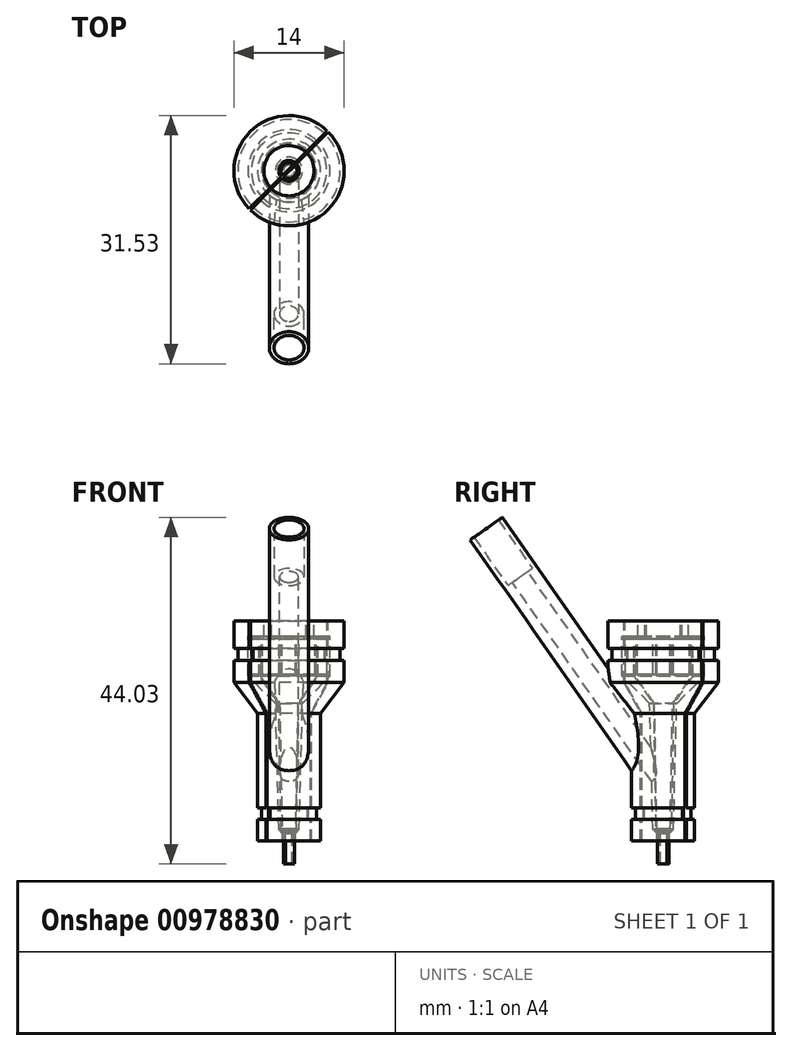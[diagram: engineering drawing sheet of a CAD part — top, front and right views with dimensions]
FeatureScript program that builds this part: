
annotation { "Feature Type Name" : "Feature", "Feature Type Description" : "" }
export const myFeature = defineFeature(function(context is Context, id is Id, definition is map)
    precondition{}
    {
        {
            var Q0;
            Q0=qCreatedBy(makeId("Front.planeOp"),FACE);
            var sketch = newSketch(context, id + "F0", { "sketchPlane" : qUnion([Q0])});
            skLineSegment(sketch, "E0", {"start": v(0, -7) * mm, "end": v(0.7, -7) * mm});
            skLineSegment(sketch, "E1", {"start": v(0.7, -7) * mm, "end": v(0.7, -2.83) * mm});
            skLineSegment(sketch, "E2", {"start": v(0.7, -2.83) * mm, "end": v(1, -2.83) * mm});
            skLineSegment(sketch, "E3", {"start": v(1, -2.83) * mm, "end": v(1, -2.58) * mm});
            skLineSegment(sketch, "E4", {"start": v(1, -2.58) * mm, "end": v(0, -2.58) * mm});
            skLineSegment(sketch, "E5", {"start": v(0, -2.58) * mm, "end": v(0, -7) * mm});
            skLineSegment(sketch, "E6", {"start": v(0, 0.49) * mm, "end": v(0, -9.16) * mm});
            skSolve(sketch);
        }
        {
            var Q0;
            Q0 = qSketchRegion(id + "F0", true);
            var Q1;
            Q1=sQuery(id+"F0.wireOp",EDGE,"E6");
            revolve(context, id + "F1", {"surfaceOperationType" : NewSurfaceOperationType.NEW, "entities" : qUnion([Q0]), "axis" : qUnion([Q1]), "revolveType" : RevolveType.FULL});
        }
        {
            var Q0;
            Q0=qCreatedBy(makeId("Front.planeOp"),FACE);
            var sketch = newSketch(context, id + "F2", { "sketchPlane" : qUnion([Q0])});
            skLineSegment(sketch, "E7", {"start": v(0.8, -3.1) * mm, "end": v(1.3, -2.6) * mm});
            skLineSegment(sketch, "E8", {"start": v(0.8, -3.1) * mm, "end": v(0.8, -4.1) * mm});
            skLineSegment(sketch, "E9", {"start": v(0.8, -4.1) * mm, "end": v(4, -4.1) * mm});
            skLineSegment(sketch, "E10", {"start": v(1.72, 13.38) * mm, "end": v(5.2, 16.87) * mm});
            skLineSegment(sketch, "E11", {"start": v(7, 23.87) * mm, "end": v(3.2, 23.87) * mm});
            skLineSegment(sketch, "E12", {"start": v(3.2, 21.87) * mm, "end": v(3.2, 23.87) * mm});
            skLineSegment(sketch, "E13", {"start": v(3.2, 21.87) * mm, "end": v(5.2, 21.87) * mm});
            skLineSegment(sketch, "E14", {"start": v(5.2, 21.87) * mm, "end": v(5.2, 16.87) * mm});
            skLineSegment(sketch, "E15", {"start": v(1.3, -2.6) * mm, "end": v(1.72, 13.38) * mm});
            skLineSegment(sketch, "E16.bottom", {"start": v(4.8, 21.59) * mm, "end": v(1.3, 21.59) * mm});
            skLineSegment(sketch, "E16.top", {"start": v(4.8, 17.09) * mm, "end": v(1.3, 17.09) * mm});
            skLineSegment(sketch, "E16.left", {"start": v(4.8, 21.59) * mm, "end": v(4.8, 17.09) * mm});
            skLineSegment(sketch, "E16.right", {"start": v(1.3, 21.59) * mm, "end": v(1.3, 17.09) * mm});
            skLineSegment(sketch, "E17", {"start": v(0, 34.31) * mm, "end": v(0, -20.8) * mm});
            skLineSegment(sketch, "E18", {"start": v(7, 23.87) * mm, "end": v(7, 20.36) * mm});
            skLineSegment(sketch, "E19", {"start": v(7, 20.36) * mm, "end": v(6.5, 20.36) * mm});
            skLineSegment(sketch, "E20", {"start": v(6.5, 20.36) * mm, "end": v(6.5, 18.86) * mm});
            skLineSegment(sketch, "E21", {"start": v(6.5, 18.86) * mm, "end": v(7, 18.86) * mm});
            skLineSegment(sketch, "E22", {"start": v(7, 18.86) * mm, "end": v(7, 16.04) * mm});
            skLineSegment(sketch, "E23", {"start": v(4, 12.13) * mm, "end": v(4, 0.13) * mm});
            skLineSegment(sketch, "E24", {"start": v(4, 0.13) * mm, "end": v(3.5, 0.14) * mm});
            skLineSegment(sketch, "E25", {"start": v(3.5, 0.14) * mm, "end": v(3.5, -1.36) * mm});
            skLineSegment(sketch, "E26", {"start": v(3.5, -1.36) * mm, "end": v(4, -1.37) * mm});
            skLineSegment(sketch, "E27", {"start": v(4, -1.37) * mm, "end": v(4, -4.1) * mm});
            skLineSegment(sketch, "E28", {"start": v(4, 12.13) * mm, "end": v(7, 16.04) * mm});
            skSolve(sketch);
        }
        {
            var Q0;
            Q0=makeQuery(id+"F2.imprint","IMPRINT",FACE,{"disambiguationData":[TD([[makeQuery(id+"F2.imprint","IMPRINT",EDGE,{"derivedFrom":sQuery(id+"F2.wireOp",EDGE,"E7")}),-1.0]])]});
            var Q1;
            Q1=makeQuery(id+"F2.imprint","IMPRINT",FACE,{"disambiguationData":[TD([[makeQuery(id+"F2.imprint","IMPRINT",EDGE,{"derivedFrom":sQuery(id+"F2.wireOp",EDGE,"E16.bottom")}),1.0]])]});
            var Q2;
            Q2=sQuery(id+"F2.wireOp",EDGE,"E17");
            revolve(context, id + "F3", {"surfaceOperationType" : NewSurfaceOperationType.NEW, "entities" : qUnion([Q0, Q1]), "axis" : qUnion([Q2]), "revolveType" : RevolveType.FULL});
        }
        {
            var Q0;
            Q0=sQuery(id+"F2.wireOp",EDGE,"E11");
            cPlane(context, id + "F4", {"entities" : qUnion([Q0]), "cplaneType" : CPlaneType.LINE_ANGLE, "offset" : 25 * mm, "angle" : 55 * degree, "width" : 150 * mm, "height" : 150 * mm});
        }
        {
            var Q0;
            Q0=qCreatedBy(id+"F4.planeOp",FACE);
            var sketch = newSketch(context, id + "F5", { "sketchPlane" : qUnion([Q0])});
            skCircle(sketch, "E29", {"center": v(0, 2) * mm, "radius": 1.05 * mm});
            skSolve(sketch);
        }
        {
            var Q0;
            Q0 = qSketchRegion(id + "F5", true);
            extrude(context, id + "F6", {"entities" : qUnion([Q0]), "operationType" : NewBodyOperationType.ADD, "depth" : 15 * mm, "offsetDistance" : 25 * mm, "hasSecondDirection" : true, "secondDirectionOppositeDirection" : true, "secondDirectionDepth" : -2 * mm});
        }
        {
            var Q0;
            Q0=makeQuery(id+"F6.opExtrude","CAP_FACE",FACE,{"disambiguationData":[OSD([sQuery(id+"F5.wireOp",EDGE,"E29")])],"isStart":false});
            var sketch = newSketch(context, id + "F7", { "sketchPlane" : qUnion([Q0])});
            skCircle(sketch, "E30", {"center": v(0, 2) * mm, "radius": 2.5 * mm});
            skSolve(sketch);
        }
        {
            var Q0;
            Q0=makeQuery(id+"F7.imprint","IMPRINT",FACE,{"disambiguationData":[TD([[makeQuery(id+"F7.imprint","IMPRINT",EDGE,{"derivedFrom":sQuery(id+"F7.wireOp",EDGE,"E30")}),1.0]])]});
            var Q1;
            Q1=makeQuery(id+"F3.opRevolve","SWEPT_BODY",BODY,{"disambiguationData":[OSD([sQuery(id+"F2.wireOp",EDGE,"E7"),sQuery(id+"F2.wireOp",EDGE,"E8"),sQuery(id+"F2.wireOp",EDGE,"E9"),sQuery(id+"F2.wireOp",EDGE,"E10"),sQuery(id+"F2.wireOp",EDGE,"E11"),sQuery(id+"F2.wireOp",EDGE,"E12"),sQuery(id+"F2.wireOp",EDGE,"E13"),sQuery(id+"F2.wireOp",EDGE,"E14"),sQuery(id+"F2.wireOp",EDGE,"E15"),sQuery(id+"F2.wireOp",EDGE,"E18"),sQuery(id+"F2.wireOp",EDGE,"E19"),sQuery(id+"F2.wireOp",EDGE,"E20"),sQuery(id+"F2.wireOp",EDGE,"E21"),sQuery(id+"F2.wireOp",EDGE,"E22"),sQuery(id+"F2.wireOp",EDGE,"E23"),sQuery(id+"F2.wireOp",EDGE,"E24"),sQuery(id+"F2.wireOp",EDGE,"E25"),sQuery(id+"F2.wireOp",EDGE,"E26"),sQuery(id+"F2.wireOp",EDGE,"E27"),sQuery(id+"F2.wireOp",EDGE,"E28")])]});
            extrude(context, id + "F8", {"entities" : qUnion([Q0]), "operationType" : NewBodyOperationType.ADD, "endBound" : BoundingType.UP_TO_BODY, "oppositeDirection" : true, "depth" : 25 * mm, "endBoundEntityBody" : qUnion([Q1]), "offsetDistance" : 25 * mm});
        }
        {
            var Q0;
            {var subQ0=sQuery(id+"F5.wireOp",EDGE,"E29");Q0=makeQuery(id+"F8.boolean.opBoolean","MERGE",FACE,{"derivedFrom":[makeQuery(id+"F6.opExtrude","CAP_FACE",FACE,{"disambiguationData":[OSD([subQ0])],"isStart":false}),makeQuery(id+"F8.opExtrude","CAP_FACE",FACE,{"disambiguationData":[OSD([subQ0,sQuery(id+"F7.wireOp",EDGE,"E30")])],"isStart":true})]});}
            var sketch = newSketch(context, id + "F9", { "sketchPlane" : qUnion([Q0])});
            skCircle(sketch, "E31", {"center": v(0, 2) * mm, "radius": 1.2 * mm});
            skSolve(sketch);
        }
        {
            var Q0;
            Q0=makeQuery(id+"F9.imprint","IMPRINT",FACE,{"disambiguationData":[TD([[makeQuery(id+"F9.imprint","IMPRINT",EDGE,{"derivedFrom":sQuery(id+"F9.wireOp",EDGE,"E31")}),-1.0]])]});
            var sketch = newSketch(context, id + "F10", { "sketchPlane" : qUnion([Q0])});
            skSolve(sketch);
        }
        {
            var Q0;
            Q0=makeQuery(id+"F10.imprint","IMPRINT",FACE,{"disambiguationData":[TD([[makeQuery(id+"F10.imprint","IMPRINT",EDGE,{"derivedFrom":makeQuery(id+"F9.imprint","IMPRINT",EDGE,{"derivedFrom":sQuery(id+"F9.wireOp",EDGE,"E31")})}),1.0]])]});
            var Q1;
            Q1=sQuery(id+"F9.wireOp",EDGE,"E31");
            extrude(context, id + "F11", {"entities" : qUnion([Q0]), "operationType" : NewBodyOperationType.REMOVE, "surfaceOperationType" : NewSurfaceOperationType.ADD, "surfaceEntities" : qUnion([Q1]), "oppositeDirection" : true, "depth" : 32 * mm, "offsetDistance" : 25 * mm});
        }
        {
            var Q0;
            {var subQ0=sQuery(id+"F5.wireOp",EDGE,"E29");Q0=makeQuery(id+"F8.boolean.opBoolean","MERGE",FACE,{"derivedFrom":[makeQuery(id+"F6.opExtrude","CAP_FACE",FACE,{"disambiguationData":[OSD([subQ0])],"isStart":false}),makeQuery(id+"F8.opExtrude","CAP_FACE",FACE,{"disambiguationData":[OSD([subQ0,sQuery(id+"F7.wireOp",EDGE,"E30")])],"isStart":true})]});}
            var sketch = newSketch(context, id + "F12", { "sketchPlane" : qUnion([Q0])});
            skCircle(sketch, "E32", {"center": v(0, 2) * mm, "radius": 1.9 * mm});
            skSolve(sketch);
        }
        {
            var Q0;
            Q0=makeQuery(id+"F12.imprint","IMPRINT",FACE,{"disambiguationData":[TD([[makeQuery(id+"F12.imprint","IMPRINT",EDGE,{"derivedFrom":sQuery(id+"F12.wireOp",EDGE,"E32")}),-1.0]])]});
            extrude(context, id + "F13", {"entities" : qUnion([Q0]), "operationType" : NewBodyOperationType.ADD, "depth" : 7.5 * mm, "offsetDistance" : 25 * mm});
        }
        {
            var Q0;
            Q0=makeQuery(id+"F3.opRevolve","SWEPT_FACE",FACE,{"disambiguationData":[OSD([sQuery(id+"F2.wireOp",EDGE,"E11")])]});
            var sketch = newSketch(context, id + "F14", { "sketchPlane" : qUnion([Q0])});
            skPoint(sketch, "E33.middle", {"position": v(0, 0) * mm});
            skLineSegment(sketch, "E34", {"start": v(7.9, 8.11) * mm, "end": v(-8.93, -8.7) * mm});
            skLineSegment(sketch, "E35", {"start": v(-8.93, -8.7) * mm, "end": v(-8.93, -9) * mm});
            skLineSegment(sketch, "E36", {"start": v(-8.93, -9) * mm, "end": v(8.16, 8.1) * mm});
            skLineSegment(sketch, "E37", {"start": v(8.16, 8.1) * mm, "end": v(7.9, 8.11) * mm});
            skSolve(sketch);
        }
        {
            var Q0;
            Q0 = qSketchRegion(id + "F14", true);
            extrude(context, id + "F15", {"entities" : qUnion([Q0]), "operationType" : NewBodyOperationType.REMOVE, "oppositeDirection" : true, "depth" : 55 * mm, "offsetDistance" : 25 * mm});
        }
        {
            var Q0;
            Q0 = qSketchRegion(id + "F14", true);
            extrude(context, id + "F16", {"entities" : qUnion([Q0]), "operationType" : NewBodyOperationType.REMOVE, "oppositeDirection" : true, "depth" : 55 * mm, "offsetDistance" : 25 * mm});
        }
    });
